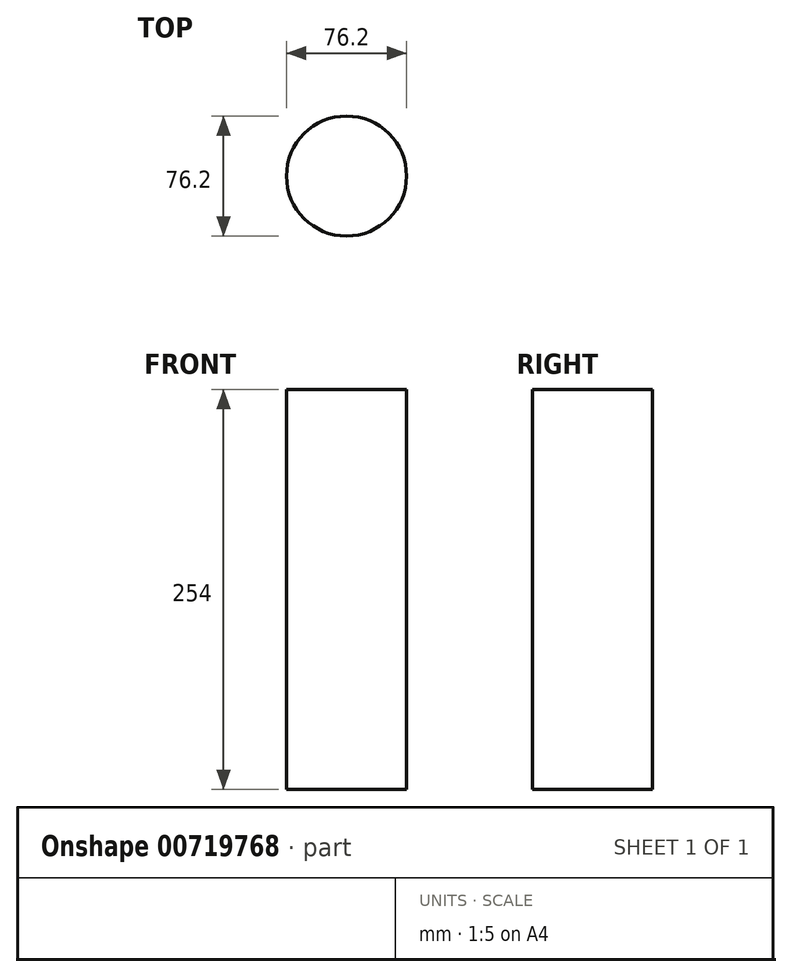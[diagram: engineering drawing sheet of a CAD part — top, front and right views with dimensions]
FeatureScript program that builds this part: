
annotation { "Feature Type Name" : "Feature", "Feature Type Description" : "" }
export const myFeature = defineFeature(function(context is Context, id is Id, definition is map)
    precondition{}
    {
        {
            var Q0;
            Q0=qCreatedBy(makeId("Top.planeOp"),FACE);
            var sketch = newSketch(context, id + "F0", { "sketchPlane" : qUnion([Q0])});
            skCircle(sketch, "E0", {"center": v(114.76, -40.81) * mm, "radius": 38.1 * mm});
            skSolve(sketch);
        }
        {
            var Q0;
            Q0 = qSketchRegion(id + "F0", true);
            extrude(context, id + "F1", {"entities" : qUnion([Q0]), "depth" : 254 * mm, "offsetDistance" : 25.4 * mm});
        }
    });
